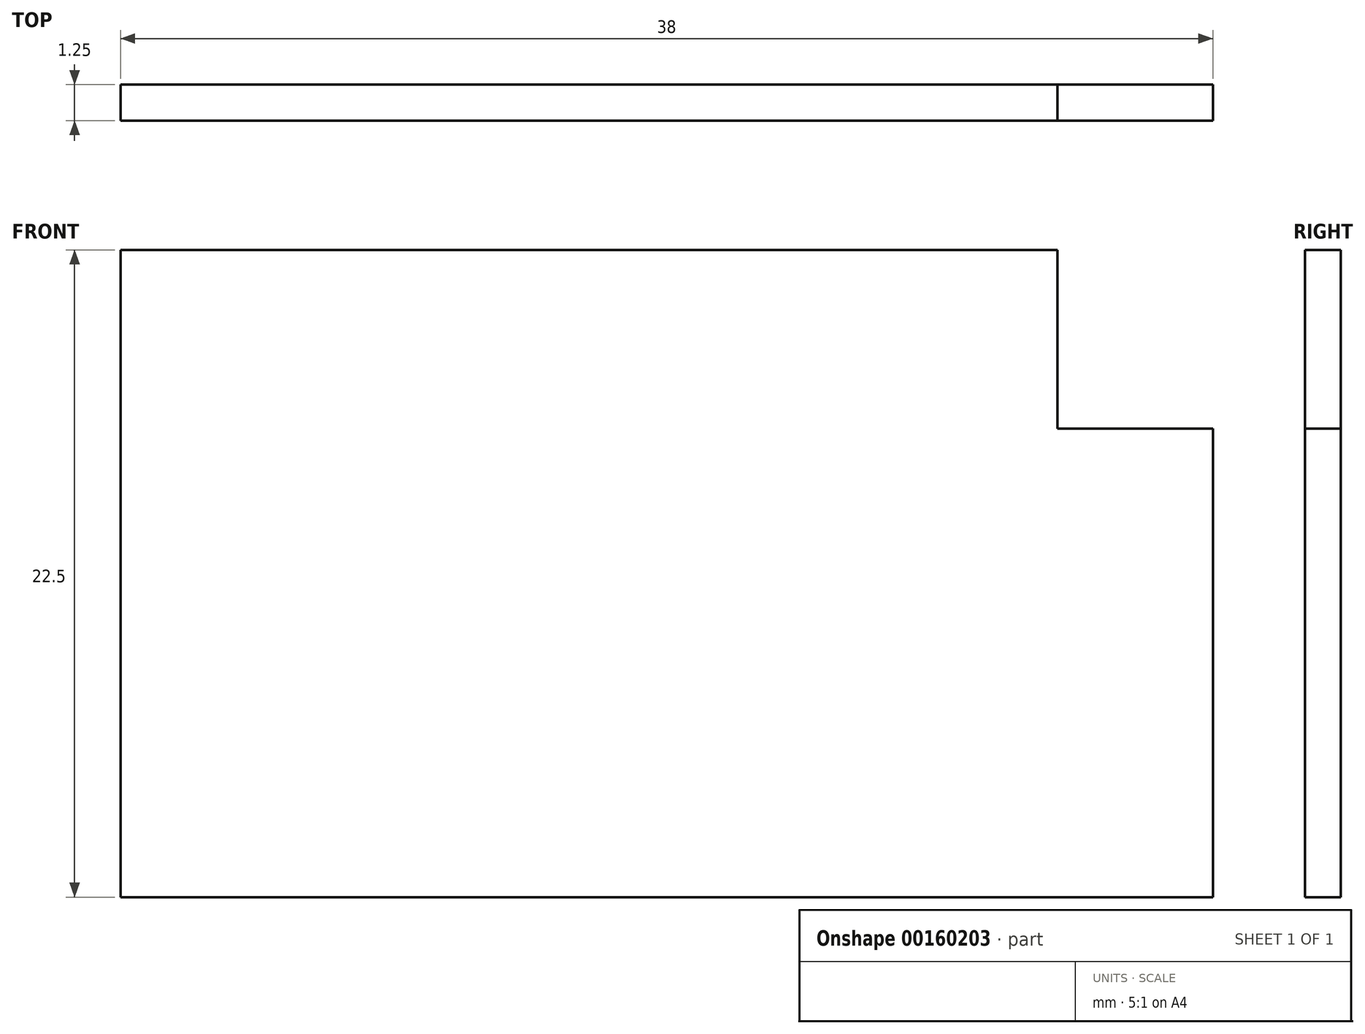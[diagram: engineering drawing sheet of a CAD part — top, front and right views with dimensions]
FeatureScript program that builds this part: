
annotation { "Feature Type Name" : "Feature", "Feature Type Description" : "" }
export const myFeature = defineFeature(function(context is Context, id is Id, definition is map)
    precondition{}
    {
        {
            var Q0;
            Q0=qCreatedBy(makeId("Front.planeOp"),FACE);
            var sketch = newSketch(context, id + "F0", { "sketchPlane" : qUnion([Q0])});
            skLineSegment(sketch, "E0.bottom", {"start": v(19, -11.25) * mm, "end": v(-19, -11.25) * mm});
            skLineSegment(sketch, "E0.top", {"start": v(19, 11.25) * mm, "end": v(-19, 11.25) * mm});
            skLineSegment(sketch, "E0.left", {"start": v(19, -11.25) * mm, "end": v(19, 11.25) * mm});
            skLineSegment(sketch, "E0.right", {"start": v(-19, -11.25) * mm, "end": v(-19, 11.25) * mm});
            skPoint(sketch, "E0.middle", {"position": v(0, 0) * mm});
            skLineSegment(sketch, "E1", {"start": v(13.59, 11.25) * mm, "end": v(13.59, 5.04) * mm});
            skLineSegment(sketch, "E2", {"start": v(13.59, 5.04) * mm, "end": v(19, 5.04) * mm});
            skSolve(sketch);
        }
        {
            var Q0;
            {var subQ2=sQuery(id+"F0.wireOp",EDGE,"E0.bottom");Q0=makeQuery(id+"F0.imprint","IMPRINT",FACE,{"disambiguationData":[TD([[makeQuery(id+"F0.imprint","IMPRINT",EDGE,{"derivedFrom":subQ2}),-1.0]])]});}
            extrude(context, id + "F1", {"entities" : qUnion([Q0]), "depth" : 1.25 * mm});
        }
    });
